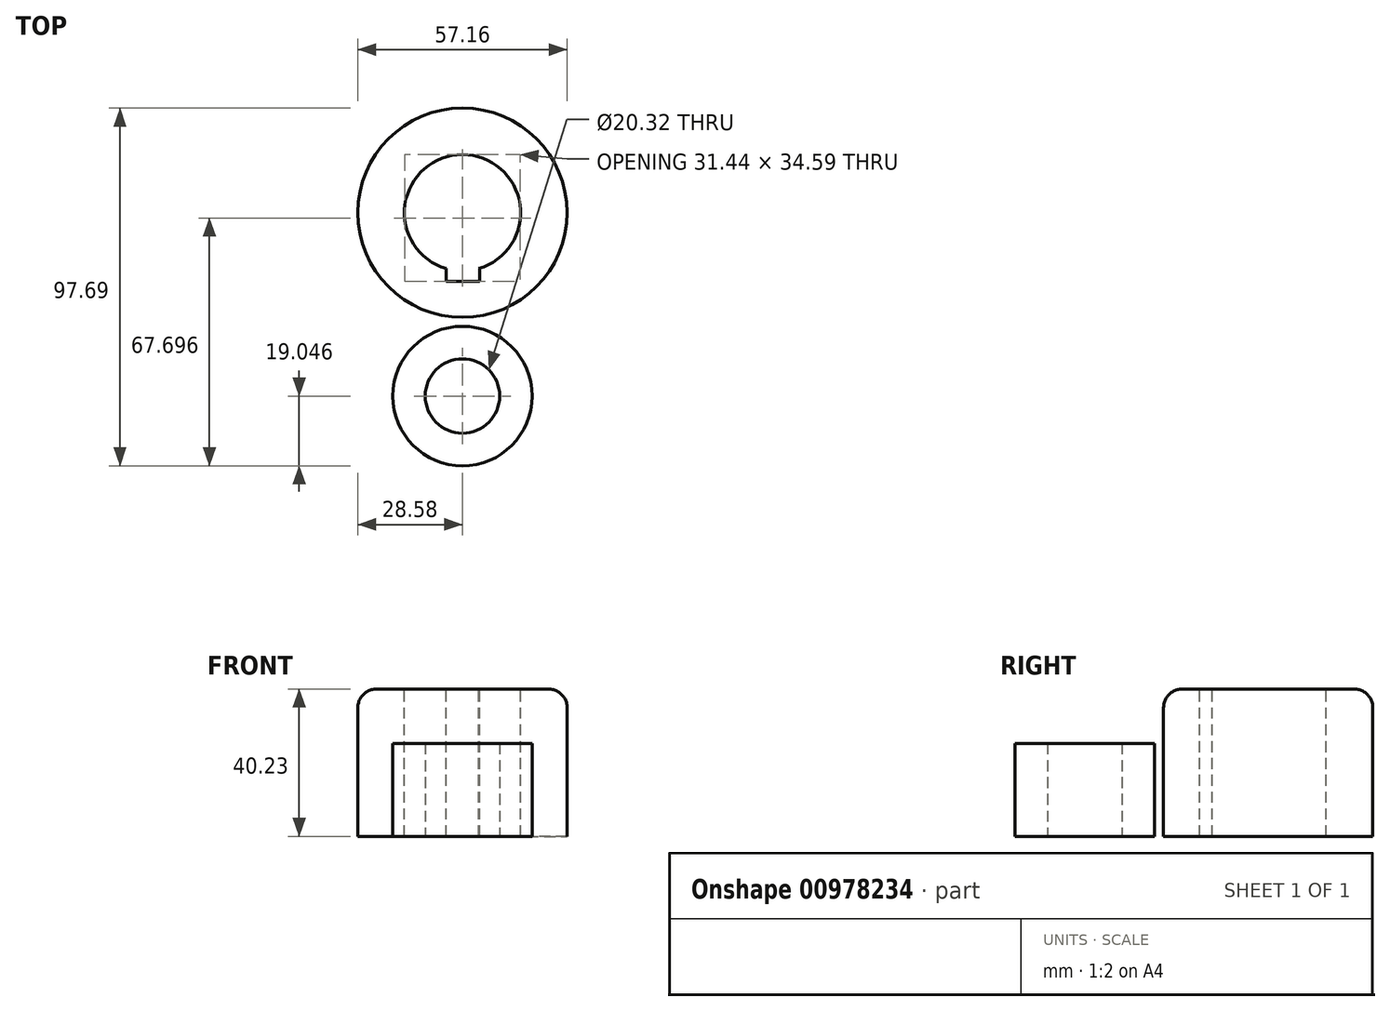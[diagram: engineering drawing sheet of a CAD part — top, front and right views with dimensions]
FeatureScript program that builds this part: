
annotation { "Feature Type Name" : "Feature", "Feature Type Description" : "" }
export const myFeature = defineFeature(function(context is Context, id is Id, definition is map)
    precondition{}
    {
        {
            var Q0;
            Q0=qCreatedBy(makeId("Top.planeOp"),FACE);
            var sketch = newSketch(context, id + "F0", { "sketchPlane" : qUnion([Q0])});
            skCircle(sketch, "E0", {"center": v(0, 54.47) * mm, "radius": 28.58 * mm});
            skSolve(sketch);
        }
        {
            var Q0;
            Q0=makeQuery(id+"F0.imprint","IMPRINT",FACE,{"disambiguationData":[TD([[makeQuery(id+"F0.imprint","IMPRINT",EDGE,{"derivedFrom":sQuery(id+"F0.wireOp",EDGE,"E0")}),1.0]])]});
            extrude(context, id + "F1", {"entities" : qUnion([Q0]), "depth" : 40.23 * mm, "offsetDistance" : 25.4 * mm});
        }
        {
            var Q0;
            Q0=makeQuery(id+"F1.opExtrude","CAP_EDGE",EDGE,{"disambiguationData":[OSD([sQuery(id+"F0.wireOp",EDGE,"E0")])],"isStart":false});
            fillet(context, id + "F2", {"entities" : qUnion([Q0]), "radius" : 5.08 * mm, "tangentPropagation" : true, "allowEdgeOverflow" : false});
        }
        {
            var Q0;
            Q0=makeQuery(id+"F1.opExtrude","CAP_FACE",FACE,{"disambiguationData":[OSD([sQuery(id+"F0.wireOp",EDGE,"E0")])],"isStart":false});
            var sketch = newSketch(context, id + "F3", { "sketchPlane" : qUnion([Q0])});
            skCircle(sketch, "E1", {"center": v(0, 54.47) * mm, "radius": 15.88 * mm});
            skLineSegment(sketch, "E2.bottom", {"start": v(-4.4, 39.22) * mm, "end": v(4.96, 39.22) * mm});
            skLineSegment(sketch, "E2.top", {"start": v(-4.4, 36.35) * mm, "end": v(4.96, 36.35) * mm});
            skLineSegment(sketch, "E2.left", {"start": v(-4.4, 39.22) * mm, "end": v(-4.4, 36.35) * mm});
            skLineSegment(sketch, "E2.right", {"start": v(4.96, 39.22) * mm, "end": v(4.96, 36.35) * mm});
            skSolve(sketch);
        }
        {
            var Q0;
            {var subQ0=sQuery(id+"F3.wireOp",EDGE,"E2.bottom");var subQ1=sQuery(id+"F3.wireOp",EDGE,"E1");var subQ3=makeQuery(id+"F3.imprint","INTERSECT",VERTEX,{"derivedFrom":[subQ1,subQ0]});Q0=makeQuery(id+"F3.imprint","IMPRINT",FACE,{"disambiguationData":[TD([[makeQuery(id+"F3.imprint","IMPRINT",EDGE,{"disambiguationData":[TD([[subQ3,-1.0]])],"derivedFrom":subQ1}),1.0]])]});}
            extrude(context, id + "F4", {"entities" : qUnion([Q0]), "operationType" : NewBodyOperationType.REMOVE, "oppositeDirection" : true, "depth" : 50.8 * mm, "offsetDistance" : 25.4 * mm});
        }
        {
            var Q0;
            Q0=makeQuery(id+"F1.opExtrude","CAP_FACE",FACE,{"disambiguationData":[OSD([sQuery(id+"F0.wireOp",EDGE,"E0")])],"isStart":false});
            var sketch = newSketch(context, id + "F5", { "sketchPlane" : qUnion([Q0])});
            skLineSegment(sketch, "E3.bottom", {"start": v(-4.4, 39.22) * mm, "end": v(4.66, 39.22) * mm});
            skLineSegment(sketch, "E3.top", {"start": v(-4.4, 35.75) * mm, "end": v(4.66, 35.75) * mm});
            skLineSegment(sketch, "E3.left", {"start": v(-4.4, 39.22) * mm, "end": v(-4.4, 35.75) * mm});
            skLineSegment(sketch, "E3.right", {"start": v(4.66, 39.22) * mm, "end": v(4.66, 35.75) * mm});
            skSolve(sketch);
        }
        {
            var Q0;
            Q0=makeQuery(id+"F5.imprint","IMPRINT",FACE,{"disambiguationData":[TD([[makeQuery(id+"F5.imprint","IMPRINT",EDGE,{"derivedFrom":sQuery(id+"F5.wireOp",EDGE,"E3.top")}),1.0]])]});
            extrude(context, id + "F6", {"entities" : qUnion([Q0]), "operationType" : NewBodyOperationType.REMOVE, "oppositeDirection" : true, "depth" : 50.8 * mm, "offsetDistance" : 25.4 * mm});
        }
        {
            var Q0;
            Q0=qCreatedBy(makeId("Top.planeOp"),FACE);
            var sketch = newSketch(context, id + "F7", { "sketchPlane" : qUnion([Q0])});
            skCircle(sketch, "E4", {"center": v(0, 4.4) * mm, "radius": 10.16 * mm});
            skCircle(sketch, "E5", {"center": v(0, 4.4) * mm, "radius": 19.05 * mm});
            skSolve(sketch);
        }
        {
            var Q0;
            Q0=makeQuery(id+"F7.imprint","IMPRINT",FACE,{"disambiguationData":[TD([[makeQuery(id+"F7.imprint","IMPRINT",EDGE,{"derivedFrom":sQuery(id+"F7.wireOp",EDGE,"E4")}),-1.0]])]});
            extrude(context, id + "F8", {"entities" : qUnion([Q0]), "depth" : 25.4 * mm, "offsetDistance" : 25.4 * mm});
        }
    });
